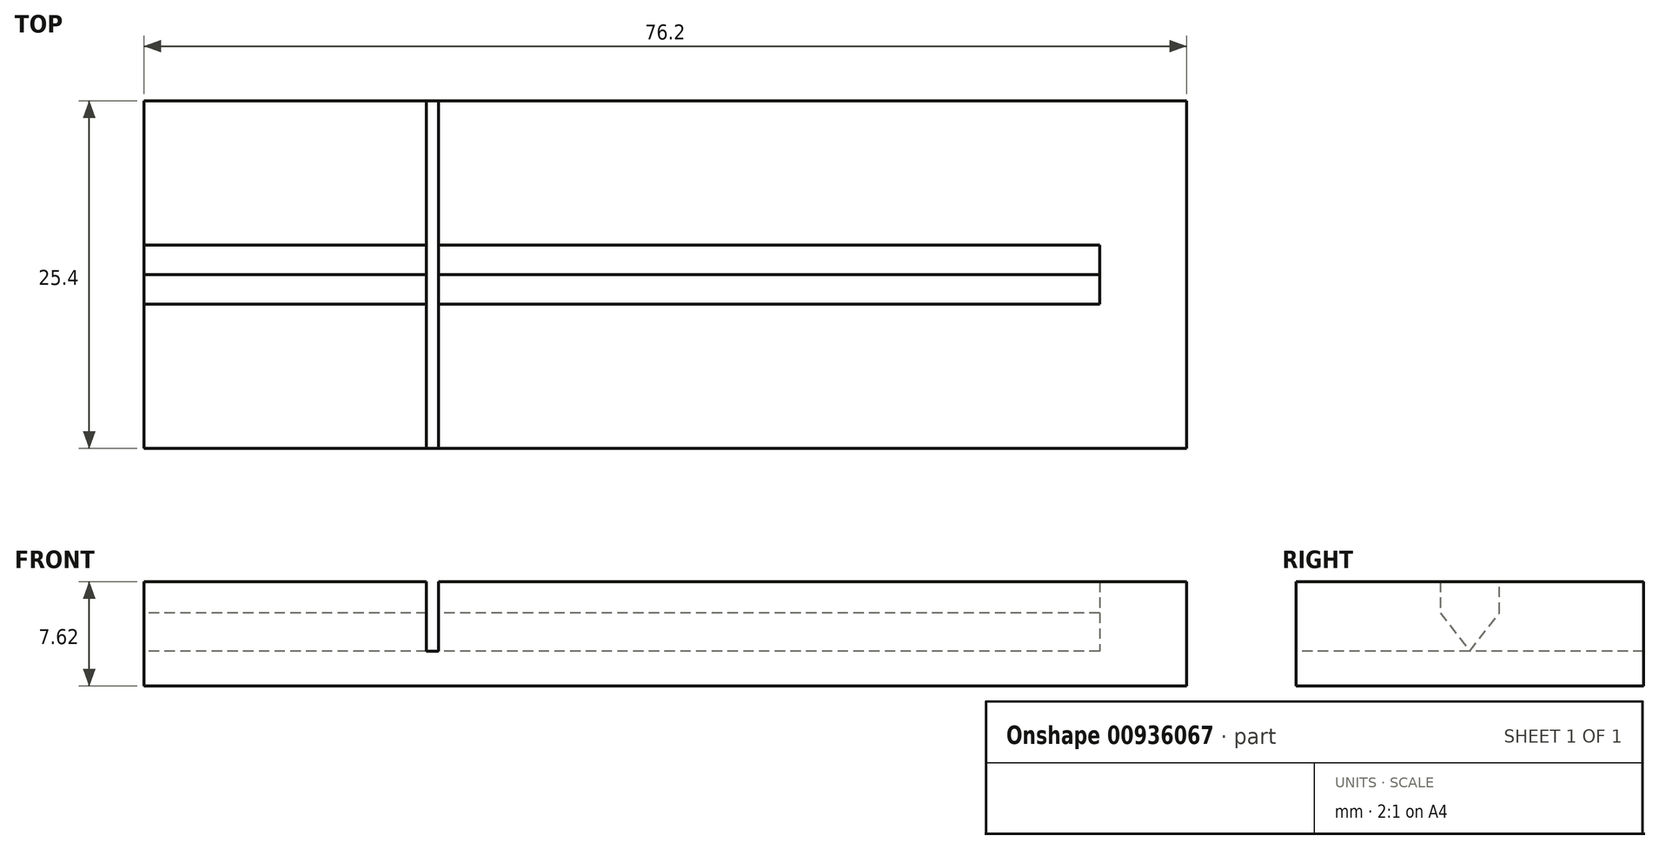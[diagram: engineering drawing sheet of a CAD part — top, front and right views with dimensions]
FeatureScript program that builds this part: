
annotation { "Feature Type Name" : "Feature", "Feature Type Description" : "" }
export const myFeature = defineFeature(function(context is Context, id is Id, definition is map)
    precondition{}
    {
        {
            var Q0;
            Q0=qCreatedBy(makeId("Top.planeOp"),FACE);
            var sketch = newSketch(context, id + "F0", { "sketchPlane" : qUnion([Q0])});
            skLineSegment(sketch, "E0.bottom", {"start": v(38.1, -12.7) * mm, "end": v(-38.1, -12.7) * mm});
            skLineSegment(sketch, "E0.top", {"start": v(38.1, 12.7) * mm, "end": v(-38.1, 12.7) * mm});
            skLineSegment(sketch, "E0.left", {"start": v(38.1, -12.7) * mm, "end": v(38.1, 12.7) * mm});
            skLineSegment(sketch, "E0.right", {"start": v(-38.1, -12.7) * mm, "end": v(-38.1, 12.7) * mm});
            skPoint(sketch, "E0.middle", {"position": v(0, 0) * mm});
            skSolve(sketch);
        }
        {
            var Q0;
            Q0 = qSketchRegion(id + "F0", true);
            extrude(context, id + "F1", {"entities" : qUnion([Q0]), "depth" : 7.62 * mm, "offsetDistance" : 25.4 * mm});
        }
        {
            var Q0;
            Q0=makeQuery(id+"F1.opExtrude","SWEPT_FACE",FACE,{"disambiguationData":[OSD([sQuery(id+"F0.wireOp",EDGE,"E0.right")])]});
            var sketch = newSketch(context, id + "F2", { "sketchPlane" : qUnion([Q0])});
            skLineSegment(sketch, "E1", {"start": v(-2.16, 7.62) * mm, "end": v(-2.16, 5.35) * mm});
            skLineSegment(sketch, "E2", {"start": v(-2.16, 5.35) * mm, "end": v(0, 2.54) * mm});
            skLineSegment(sketch, "E3", {"start": v(0, 2.54) * mm, "end": v(2.16, 5.35) * mm});
            skLineSegment(sketch, "E4", {"start": v(2.16, 5.35) * mm, "end": v(2.16, 7.62) * mm});
            skLineSegment(sketch, "E5", {"start": v(2.16, 7.62) * mm, "end": v(-2.16, 7.62) * mm});
            skCircle(sketch, "E6", {"center": v(0, 4.42) * mm, "radius": 1.74 * mm, "construction": true});
            skSolve(sketch);
        }
        {
            var Q0;
            Q0 = qSketchRegion(id + "F2", true);
            extrude(context, id + "F3", {"entities" : qUnion([Q0]), "operationType" : NewBodyOperationType.REMOVE, "oppositeDirection" : true, "depth" : 69.85 * mm, "offsetDistance" : 25.4 * mm});
        }
        {
            var Q0;
            Q0=makeQuery(id+"F1.opExtrude","CAP_FACE",FACE,{"disambiguationData":[OSD([sQuery(id+"F0.wireOp",EDGE,"E0.bottom"),sQuery(id+"F0.wireOp",EDGE,"E0.top"),sQuery(id+"F0.wireOp",EDGE,"E0.left"),sQuery(id+"F0.wireOp",EDGE,"E0.right")])],"isStart":false});
            var sketch = newSketch(context, id + "F4", { "sketchPlane" : qUnion([Q0])});
            skLineSegment(sketch, "E7.bottom", {"start": v(-17.45, 12.7) * mm, "end": v(-16.59, 12.7) * mm});
            skLineSegment(sketch, "E7.top", {"start": v(-17.45, -12.7) * mm, "end": v(-16.59, -12.7) * mm});
            skLineSegment(sketch, "E7.left", {"start": v(-17.45, 12.7) * mm, "end": v(-17.45, -12.7) * mm});
            skLineSegment(sketch, "E7.right", {"start": v(-16.59, 12.7) * mm, "end": v(-16.59, -12.7) * mm});
            skPoint(sketch, "E7.middle", {"position": v(-17.02, 0) * mm});
            skSolve(sketch);
        }
        {
            var Q0;
            Q0 = qSketchRegion(id + "F4", true);
            extrude(context, id + "F5", {"entities" : qUnion([Q0]), "operationType" : NewBodyOperationType.REMOVE, "oppositeDirection" : true, "depth" : 5.08 * mm, "offsetDistance" : 25.4 * mm});
        }
    });
